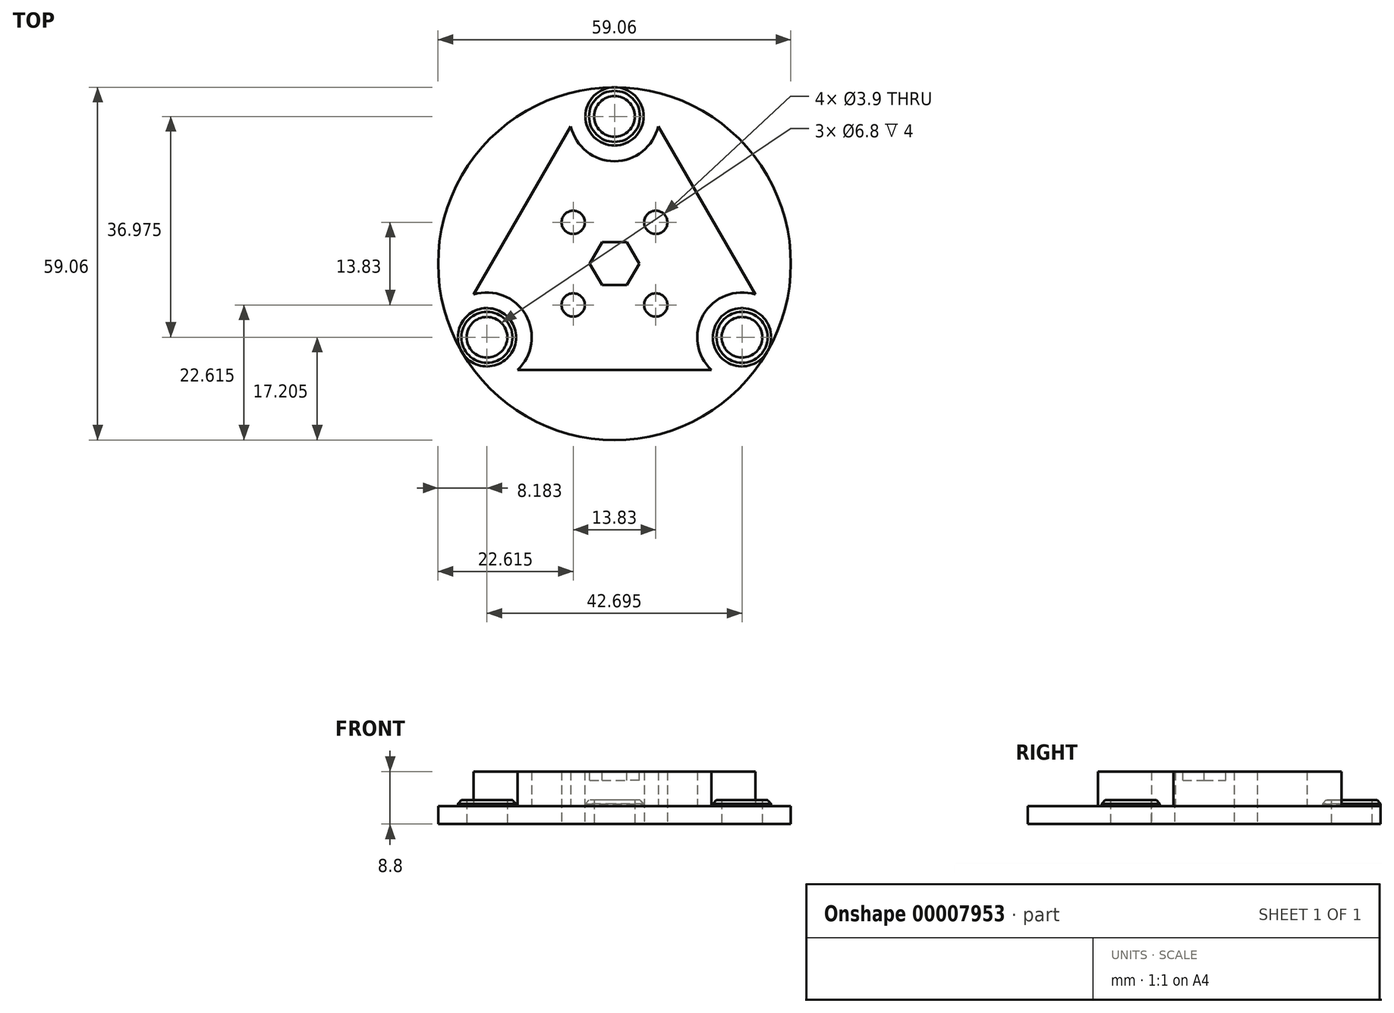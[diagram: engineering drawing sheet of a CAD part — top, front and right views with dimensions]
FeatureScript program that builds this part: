
annotation { "Feature Type Name" : "Feature", "Feature Type Description" : "" }
export const myFeature = defineFeature(function(context is Context, id is Id, definition is map)
    precondition{}
    {
        {
            var Q0;
            Q0=qCreatedBy(makeId("Top.planeOp"),FACE);
            var sketch = newSketch(context, id + "F0", { "sketchPlane" : qUnion([Q0])});
            skCircle(sketch, "E0", {"center": v(0, 0) * mm, "radius": 30 * mm, "construction": true});
            skCircle(sketch, "E1", {"center": v(0, 0) * mm, "radius": 31 * mm, "construction": true});
            skLineSegment(sketch, "E2", {"start": v(0, 30) * mm, "end": v(0, 31) * mm, "construction": true});
            skLineSegment(sketch, "E3", {"start": v(0, 30) * mm, "end": v(0, 0) * mm, "construction": true});
            skCircle(sketch, "E4", {"center": v(0, 24.65) * mm, "radius": 6.35 * mm, "construction": true});
            skCircle(sketch, "E5", {"center": v(0, 24.65) * mm, "radius": 3.4 * mm});
            skCircle(sketch, "E6.1.0", {"center": v(-21.35, -12.32) * mm, "radius": 3.4 * mm});
            skCircle(sketch, "E6.2.0", {"center": v(21.35, -12.33) * mm, "radius": 3.4 * mm});
            skLineSegment(sketch, "E7", {"start": v(-24.3, -14.02) * mm, "end": v(-26.85, -15.5) * mm, "construction": true});
            skPoint(sketch, "E8", {"position": v(-25.57, -14.76) * mm});
            skCircle(sketch, "E9", {"center": v(0, 0) * mm, "radius": 29.52 * mm});
            skSolve(sketch);
        }
        {
            var Q0;
            Q0 = qSketchRegion(id + "F0", true);
            extrude(context, id + "F1", {"entities" : qUnion([Q0]), "depth" : 3 * mm});
        }
        {
            var Q0;
            Q0=makeQuery(id+"F1.opExtrude","CAP_FACE",FACE,{"disambiguationData":[OSD([sQuery(id+"F0.wireOp",EDGE,"E5"),sQuery(id+"F0.wireOp",EDGE,"E6.1.0"),sQuery(id+"F0.wireOp",EDGE,"E6.2.0"),sQuery(id+"F0.wireOp",EDGE,"E9")])],"isStart":false});
            var sketch = newSketch(context, id + "F2", { "sketchPlane" : qUnion([Q0])});
            skCircle(sketch, "E10", {"center": v(0, 24.65) * mm, "radius": 4.88 * mm});
            skCircle(sketch, "E11", {"center": v(21.35, -12.33) * mm, "radius": 4.88 * mm});
            skCircle(sketch, "E12", {"center": v(-21.35, -12.32) * mm, "radius": 4.87 * mm});
            skCircle(sketch, "E13.0", {"center": v(0, 24.65) * mm, "radius": 3.4 * mm});
            skCircle(sketch, "E13.1", {"center": v(-21.35, -12.32) * mm, "radius": 3.4 * mm});
            skCircle(sketch, "E13.2", {"center": v(21.35, -12.33) * mm, "radius": 3.4 * mm});
            skSolve(sketch);
        }
        {
            var Q0;
            Q0 = qSketchRegion(id + "F2", true);
            extrude(context, id + "F3", {"entities" : qUnion([Q0]), "operationType" : NewBodyOperationType.ADD, "depth" : 1 * mm});
        }
        {
            var Q0;
            Q0=makeQuery(id+"F3.opExtrude","CAP_EDGE",EDGE,{"disambiguationData":[OSD([sQuery(id+"F2.wireOp",EDGE,"E12")])],"isStart":false});
            var Q1;
            Q1=makeQuery(id+"F3.opExtrude","CAP_EDGE",EDGE,{"disambiguationData":[OSD([sQuery(id+"F2.wireOp",EDGE,"E11")])],"isStart":false});
            var Q2;
            Q2=makeQuery(id+"F3.opExtrude","CAP_EDGE",EDGE,{"disambiguationData":[OSD([sQuery(id+"F2.wireOp",EDGE,"E10")])],"isStart":false});
            chamfer(context, id + "F4", {"entities" : qUnion([Q0, Q1, Q2]), "width" : 0.6 * mm, "tangentPropagation" : true});
        }
        {
            var Q0;
            Q0=makeQuery(id+"F1.opExtrude","CAP_FACE",FACE,{"disambiguationData":[OSD([sQuery(id+"F0.wireOp",EDGE,"E5"),sQuery(id+"F0.wireOp",EDGE,"E6.1.0"),sQuery(id+"F0.wireOp",EDGE,"E6.2.0"),sQuery(id+"F0.wireOp",EDGE,"E9")])],"isStart":false});
            var sketch = newSketch(context, id + "F5", { "sketchPlane" : qUnion([Q0])});
            skCircle(sketch, "E14", {"center": v(0, 24.65) * mm, "radius": 7.5 * mm, "construction": true});
            skCircle(sketch, "E15", {"center": v(-21.35, -12.32) * mm, "radius": 7.5 * mm, "construction": true});
            skCircle(sketch, "E16", {"center": v(21.35, -12.33) * mm, "radius": 7.5 * mm, "construction": true});
            skLineSegment(sketch, "E17", {"start": v(-6.5, 28.4) * mm, "end": v(-27.84, -8.58) * mm, "construction": true});
            skLineSegment(sketch, "E18", {"start": v(6.5, 28.4) * mm, "end": v(27.84, -8.58) * mm, "construction": true});
            skLineSegment(sketch, "E19", {"start": v(-21.35, -19.82) * mm, "end": v(21.35, -19.82) * mm, "construction": true});
            skLineSegment(sketch, "E20", {"start": v(-7.31, 22.98) * mm, "end": v(-23.56, -5.16) * mm});
            skLineSegment(sketch, "E21", {"start": v(7.31, 22.98) * mm, "end": v(23.56, -5.16) * mm});
            skLineSegment(sketch, "E22", {"start": v(16.25, -17.82) * mm, "end": v(-16.25, -17.82) * mm});
            skLineSegment(sketch, "E23", {"start": v(0, -17.82) * mm, "end": v(0, -19.82) * mm, "construction": true});
            skLineSegment(sketch, "E24", {"start": v(-15.44, 8.91) * mm, "end": v(-17.17, 9.91) * mm, "construction": true});
            skLineSegment(sketch, "E25", {"start": v(15.44, 8.91) * mm, "end": v(17.17, 9.91) * mm, "construction": true});
            skArc(sketch, "E26", {"start": v(-7.31, 22.98) * mm, "mid": v(0, 17.15) * mm, "end": v(7.31, 22.98) * mm});
            skArc(sketch, "E27", {"start": v(23.56, -5.16) * mm, "mid": v(14.85, -8.57) * mm, "end": v(16.25, -17.82) * mm});
            skArc(sketch, "E28", {"start": v(-16.25, -17.82) * mm, "mid": v(-14.85, -8.57) * mm, "end": v(-23.56, -5.16) * mm});
            skSolve(sketch);
        }
        {
            var Q0;
            Q0 = qSketchRegion(id + "F5", true);
            extrude(context, id + "F6", {"entities" : qUnion([Q0]), "operationType" : NewBodyOperationType.ADD, "depth" : 5.8 * mm});
        }
        {
            var Q0;
            Q0=makeQuery(id+"F1.opExtrude","CAP_FACE",FACE,{"disambiguationData":[OSD([sQuery(id+"F0.wireOp",EDGE,"E5"),sQuery(id+"F0.wireOp",EDGE,"E6.1.0"),sQuery(id+"F0.wireOp",EDGE,"E6.2.0"),sQuery(id+"F0.wireOp",EDGE,"E9")])],"isStart":true});
            var sketch = newSketch(context, id + "F7", { "sketchPlane" : qUnion([Q0])});
            skLineSegment(sketch, "E29", {"start": v(0, 0) * mm, "end": v(0, -24.65) * mm, "construction": true});
            skCircle(sketch, "E30.cCircle", {"center": v(0, 0) * mm, "radius": 9.78 * mm, "construction": true});
            skLineSegment(sketch, "E30.0", {"start": v(6.91, -6.91) * mm, "end": v(-6.91, -6.91) * mm, "construction": true});
            skLineSegment(sketch, "E30.1", {"start": v(-6.91, -6.91) * mm, "end": v(-6.91, 6.91) * mm, "construction": true});
            skLineSegment(sketch, "E30.2", {"start": v(-6.91, 6.91) * mm, "end": v(6.91, 6.91) * mm, "construction": true});
            skLineSegment(sketch, "E30.3", {"start": v(6.91, 6.91) * mm, "end": v(6.91, -6.91) * mm, "construction": true});
            skCircle(sketch, "E31", {"center": v(6.91, 6.91) * mm, "radius": 1.95 * mm});
            skCircle(sketch, "E32.1.0", {"center": v(-6.91, 6.91) * mm, "radius": 1.95 * mm});
            skCircle(sketch, "E32.2.0", {"center": v(-6.91, -6.91) * mm, "radius": 1.95 * mm});
            skCircle(sketch, "E32.3.0", {"center": v(6.91, -6.91) * mm, "radius": 1.95 * mm});
            skSolve(sketch);
        }
        {
            var Q0;
            Q0 = qSketchRegion(id + "F7", true);
            extrude(context, id + "F8", {"entities" : qUnion([Q0]), "operationType" : NewBodyOperationType.REMOVE, "endBound" : BoundingType.THROUGH_ALL, "oppositeDirection" : true, "depth" : 25 * mm});
        }
        {
            var Q0;
            Q0=makeQuery(id+"F6.opExtrude","CAP_FACE",FACE,{"disambiguationData":[OSD([sQuery(id+"F5.wireOp",EDGE,"E20"),sQuery(id+"F5.wireOp",EDGE,"E21"),sQuery(id+"F5.wireOp",EDGE,"E22"),sQuery(id+"F5.wireOp",EDGE,"b30b8c31-8519-46e4-bd01-4f495bb6e8cf"),sQuery(id+"F5.wireOp",EDGE,"E26"),sQuery(id+"F5.wireOp",EDGE,"E27")])],"isStart":false});
            var sketch = newSketch(context, id + "F9", { "sketchPlane" : qUnion([Q0])});
            skCircle(sketch, "E33.cCircle", {"center": v(0, 0) * mm, "radius": 3.6 * mm, "construction": true});
            skLineSegment(sketch, "E33.0", {"start": v(-2.08, 3.6) * mm, "end": v(2.08, 3.6) * mm});
            skLineSegment(sketch, "E33.1", {"start": v(2.08, 3.6) * mm, "end": v(4.16, 0) * mm});
            skLineSegment(sketch, "E33.2", {"start": v(4.16, 0) * mm, "end": v(2.08, -3.6) * mm});
            skLineSegment(sketch, "E33.3", {"start": v(2.08, -3.6) * mm, "end": v(-2.08, -3.6) * mm});
            skLineSegment(sketch, "E33.4", {"start": v(-2.08, -3.6) * mm, "end": v(-4.16, 0) * mm});
            skLineSegment(sketch, "E33.5", {"start": v(-4.16, 0) * mm, "end": v(-2.08, 3.6) * mm});
            skPoint(sketch, "E33.0.midPoint", {"position": v(0, 3.6) * mm});
            skSolve(sketch);
        }
        {
            var Q0;
            Q0 = qSketchRegion(id + "F9", true);
            extrude(context, id + "F10", {"entities" : qUnion([Q0]), "operationType" : NewBodyOperationType.REMOVE, "oppositeDirection" : true, "depth" : 1.45 * mm});
        }
    });
